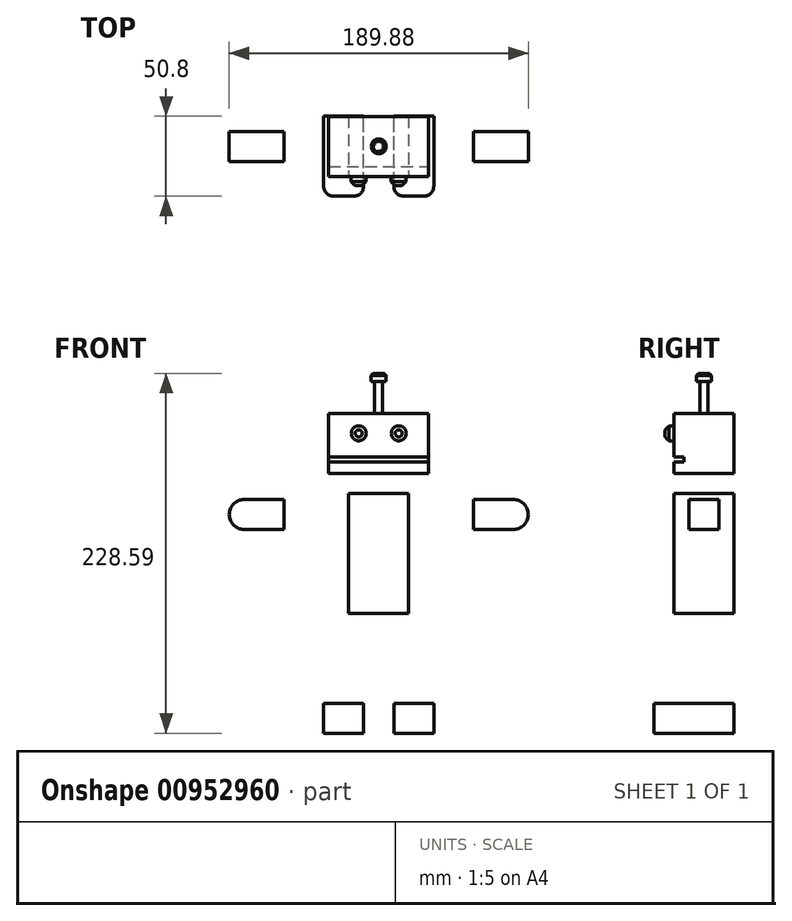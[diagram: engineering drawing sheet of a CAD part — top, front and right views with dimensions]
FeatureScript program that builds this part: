
annotation { "Feature Type Name" : "Feature", "Feature Type Description" : "" }
export const myFeature = defineFeature(function(context is Context, id is Id, definition is map)
    precondition{}
    {
        {
            var Q0;
            Q0=qCreatedBy(makeId("Top.planeOp"),FACE);
            var sketch = newSketch(context, id + "F0", { "sketchPlane" : qUnion([Q0])});
            skLineSegment(sketch, "E0.bottom", {"start": v(-19.05, 19.05) * mm, "end": v(19.05, 19.05) * mm});
            skLineSegment(sketch, "E0.top", {"start": v(-19.05, -19.05) * mm, "end": v(19.05, -19.05) * mm});
            skLineSegment(sketch, "E0.left", {"start": v(-19.05, 19.05) * mm, "end": v(-19.05, -19.05) * mm});
            skLineSegment(sketch, "E0.right", {"start": v(19.05, 19.05) * mm, "end": v(19.05, -19.05) * mm});
            skSolve(sketch);
        }
        {
            var Q0;
            Q0=makeQuery(id+"F0.imprint","IMPRINT",FACE,{"disambiguationData":[TD([[makeQuery(id+"F0.imprint","IMPRINT",EDGE,{"derivedFrom":sQuery(id+"F0.wireOp",EDGE,"E0.bottom")}),-1.0]])]});
            extrude(context, id + "F1", {"entities" : qUnion([Q0]), "depth" : 76.2 * mm, "offsetDistance" : 25.4 * mm});
        }
        {
            var Q0;
            Q0=qCreatedBy(makeId("Front.planeOp"),FACE);
            var sketch = newSketch(context, id + "F2", { "sketchPlane" : qUnion([Q0])});
            skLineSegment(sketch, "E1.bottom", {"start": v(-31.75, 126.99) * mm, "end": v(31.75, 126.99) * mm});
            skLineSegment(sketch, "E1.top", {"start": v(-31.75, 88.89) * mm, "end": v(31.75, 88.89) * mm});
            skLineSegment(sketch, "E1.left", {"start": v(-31.75, 126.99) * mm, "end": v(-31.75, 88.89) * mm});
            skLineSegment(sketch, "E1.right", {"start": v(31.75, 126.99) * mm, "end": v(31.75, 88.89) * mm});
            skSolve(sketch);
        }
        {
            var Q0;
            Q0=makeQuery(id+"F2.imprint","IMPRINT",FACE,{"disambiguationData":[TD([[makeQuery(id+"F2.imprint","IMPRINT",EDGE,{"derivedFrom":sQuery(id+"F2.wireOp",EDGE,"E1.bottom")}),-1.0]])]});
            extrude(context, id + "F3", {"entities" : qUnion([Q0]), "depth" : 19.05 * mm, "offsetDistance" : 25.4 * mm, "hasSecondDirection" : true, "secondDirectionOppositeDirection" : true, "secondDirectionDepth" : 19.05 * mm});
        }
        {
            var Q0;
            Q0=makeQuery(id+"F3.opExtrude","SWEPT_FACE",FACE,{"disambiguationData":[OSD([sQuery(id+"F2.wireOp",EDGE,"E1.right")])]});
            var sketch = newSketch(context, id + "F4", { "sketchPlane" : qUnion([Q0])});
            skLineSegment(sketch, "E2.bottom", {"start": v(-19.05, 96.06) * mm, "end": v(-12.7, 96.06) * mm});
            skLineSegment(sketch, "E2.top", {"start": v(-19.05, 99.24) * mm, "end": v(-12.7, 99.24) * mm});
            skLineSegment(sketch, "E2.left", {"start": v(-19.05, 96.06) * mm, "end": v(-19.05, 99.24) * mm});
            skLineSegment(sketch, "E2.right", {"start": v(-12.7, 96.06) * mm, "end": v(-12.7, 99.24) * mm});
            skSolve(sketch);
        }
        {
            var Q0;
            Q0=makeQuery(id+"F4.imprint","IMPRINT",FACE,{"disambiguationData":[TD([[makeQuery(id+"F4.imprint","IMPRINT",EDGE,{"derivedFrom":sQuery(id+"F4.wireOp",EDGE,"E2.bottom")}),1.0]])]});
            extrude(context, id + "F5", {"entities" : qUnion([Q0]), "operationType" : NewBodyOperationType.REMOVE, "endBound" : BoundingType.THROUGH_ALL, "oppositeDirection" : true, "depth" : 25.4 * mm, "offsetDistance" : 25.4 * mm});
        }
        {
            var Q0;
            {var subQ0=sQuery(id+"F2.wireOp",EDGE,"E1.bottom");var subQ1=sQuery(id+"F2.wireOp",EDGE,"E1.right");var subQ2=sQuery(id+"F2.wireOp",EDGE,"E1.left");Q0=makeQuery(id+"F5.boolean.opBoolean","SPLIT",FACE,{"disambiguationData":[TD([makeQuery(id+"F3.opExtrude","SWEPT_FACE",FACE,{"disambiguationData":[OSD([subQ0])]})])],"derivedFrom":makeQuery(id+"F3.opExtrude","CAP_FACE",FACE,{"disambiguationData":[OSD([subQ0,sQuery(id+"F2.wireOp",EDGE,"E1.top"),subQ2,subQ1])],"isStart":false})});}
            var sketch = newSketch(context, id + "F6", { "sketchPlane" : qUnion([Q0])});
            skCircle(sketch, "E3", {"center": v(-12.7, 114.29) * mm, "radius": 4.76 * mm});
            skCircle(sketch, "E4", {"center": v(12.7, 114.29) * mm, "radius": 4.76 * mm});
            skLineSegment(sketch, "E5", {"start": v(0, 134.8) * mm, "end": v(0, 83.98) * mm, "construction": true});
            skSolve(sketch);
        }
        {
            var Q0;
            Q0 = qSketchRegion(id + "F6", true);
            extrude(context, id + "F7", {"entities" : qUnion([Q0]), "depth" : 5.84 * mm, "offsetDistance" : 25.4 * mm});
        }
        {
            var Q0;
            Q0=makeQuery(id+"F7.opExtrude","CAP_EDGE",EDGE,{"disambiguationData":[OSD([sQuery(id+"F6.wireOp",EDGE,"E3")])],"isStart":false});
            var Q1;
            Q1=makeQuery(id+"F7.opExtrude","CAP_FACE",FACE,{"disambiguationData":[OSD([sQuery(id+"F6.wireOp",EDGE,"E4")])],"isStart":false});
            chamfer(context, id + "F8", {"entities" : qUnion([Q0, Q1]), "width" : 2.54 * mm, "tangentPropagation" : true});
        }
        {
            var Q0;
            Q0=makeQuery(id+"F3.opExtrude","SWEPT_FACE",FACE,{"disambiguationData":[OSD([sQuery(id+"F2.wireOp",EDGE,"E1.bottom")])]});
            var sketch = newSketch(context, id + "F9", { "sketchPlane" : qUnion([Q0])});
            skCircle(sketch, "E6", {"center": v(0, 0) * mm, "radius": 2.54 * mm});
            skSolve(sketch);
        }
        {
            var Q0;
            Q0 = qSketchRegion(id + "F9", true);
            extrude(context, id + "F10", {"entities" : qUnion([Q0]), "operationType" : NewBodyOperationType.ADD, "depth" : 20.32 * mm, "offsetDistance" : 25.4 * mm});
        }
        {
            var Q0;
            Q0=makeQuery(id+"F10.opExtrude","CAP_FACE",FACE,{"disambiguationData":[OSD([sQuery(id+"F9.wireOp",EDGE,"E6")])],"isStart":false});
            var sketch = newSketch(context, id + "F11", { "sketchPlane" : qUnion([Q0])});
            skCircle(sketch, "E7", {"center": v(0, 0) * mm, "radius": 4.76 * mm});
            skSolve(sketch);
        }
        {
            var Q0;
            Q0=makeQuery(id+"F11.imprint","IMPRINT",FACE,{"disambiguationData":[TD([[makeQuery(id+"F11.imprint","IMPRINT",EDGE,{"derivedFrom":sQuery(id+"F11.wireOp",EDGE,"E7")}),1.0]])]});
            var Q1;
            Q1=makeQuery(id+"F11.imprint","IMPRINT",FACE,{"disambiguationData":[TD([[makeQuery(id+"F11.imprint","IMPRINT",EDGE,{"derivedFrom":makeQuery(id+"F10.opExtrude","CAP_EDGE",EDGE,{"disambiguationData":[OSD([sQuery(id+"F9.wireOp",EDGE,"E6")])],"isStart":false})}),1.0]])]});
            extrude(context, id + "F12", {"entities" : qUnion([Q0, Q1]), "operationType" : NewBodyOperationType.ADD, "depth" : 5.08 * mm, "offsetDistance" : 25.4 * mm});
        }
        {
            var Q0;
            Q0=makeQuery(id+"F12.opExtrude","CAP_EDGE",EDGE,{"disambiguationData":[OSD([sQuery(id+"F11.wireOp",EDGE,"E7")])],"isStart":false});
            chamfer(context, id + "F13", {"entities" : qUnion([Q0]), "width" : 1.27 * mm, "tangentPropagation" : true});
        }
        {
            var Q0;
            Q0=qCreatedBy(makeId("Top.planeOp"),FACE);
            cPlane(context, id + "F14", {"entities" : qUnion([Q0]), "cplaneType" : CPlaneType.OFFSET, "offset" : 76.2 * mm, "oppositeDirection" : true, "width" : 152.4 * mm, "height" : 152.4 * mm});
        }
        {
            var Q0;
            Q0=qCreatedBy(id+"F14.planeOp",FACE);
            var sketch = newSketch(context, id + "F15", { "sketchPlane" : qUnion([Q0])});
            skLineSegment(sketch, "E8.bottom", {"start": v(-28.6, -31.7) * mm, "end": v(-15.9, -31.7) * mm});
            skLineSegment(sketch, "E8.top", {"start": v(-34.96, 19.1) * mm, "end": v(-9.56, 19.1) * mm});
            skLineSegment(sketch, "E8.left", {"start": v(-34.96, -25.35) * mm, "end": v(-34.96, 19.1) * mm});
            skLineSegment(sketch, "E8.right", {"start": v(-9.56, -25.35) * mm, "end": v(-9.56, 19.1) * mm});
            skPoint(sketch, "E9.visualSharp", {"position": v(-34.96, -31.7) * mm});
            skArc(sketch, "E9.filletArc", {"start": v(-34.96, -25.35) * mm, "mid": v(-33.1, -29.84) * mm, "end": v(-28.6, -31.7) * mm});
            skPoint(sketch, "E10.visualSharp", {"position": v(-9.56, -31.7) * mm});
            skArc(sketch, "E10.filletArc", {"start": v(-15.9, -31.7) * mm, "mid": v(-11.42, -29.84) * mm, "end": v(-9.56, -25.35) * mm});
            skLineSegment(sketch, "E11.MirrorCS", {"start": v(34.96, 19.1) * mm, "end": v(9.56, 19.1) * mm});
            skArc(sketch, "E12.MirrorCS", {"start": v(15.9, -31.7) * mm, "mid": v(11.42, -29.84) * mm, "end": v(9.56, -25.35) * mm});
            skPoint(sketch, "E13.MirrorP", {"position": v(34.96, -31.7) * mm});
            skArc(sketch, "E14.MirrorCS", {"start": v(34.96, -25.35) * mm, "mid": v(33.1, -29.84) * mm, "end": v(28.6, -31.7) * mm});
            skPoint(sketch, "E15.MirrorP", {"position": v(9.56, -31.7) * mm});
            skLineSegment(sketch, "E16.MirrorCS", {"start": v(34.96, -25.35) * mm, "end": v(34.96, 19.1) * mm});
            skLineSegment(sketch, "E17.MirrorCS", {"start": v(28.6, -31.7) * mm, "end": v(15.9, -31.7) * mm});
            skLineSegment(sketch, "E18.MirrorCS", {"start": v(9.56, -25.35) * mm, "end": v(9.56, 19.1) * mm});
            skSolve(sketch);
        }
        {
            var Q0;
            Q0=makeQuery(id+"F15.imprint","IMPRINT",FACE,{"disambiguationData":[TD([[makeQuery(id+"F15.imprint","IMPRINT",EDGE,{"derivedFrom":sQuery(id+"F15.wireOp",EDGE,"E8.bottom")}),1.0]])]});
            var Q1;
            Q1=makeQuery(id+"F15.imprint","IMPRINT",FACE,{"disambiguationData":[TD([[makeQuery(id+"F15.imprint","IMPRINT",EDGE,{"derivedFrom":sQuery(id+"F15.wireOp",EDGE,"E11.MirrorCS")}),1.0]])]});
            extrude(context, id + "F16", {"entities" : qUnion([Q0, Q1]), "depth" : 19.05 * mm, "offsetDistance" : 25.4 * mm});
        }
        {
            var Q0;
            Q0=qCreatedBy(makeId("Front.planeOp"),FACE);
            var sketch = newSketch(context, id + "F17", { "sketchPlane" : qUnion([Q0])});
            skLineSegment(sketch, "E19.bottom", {"start": v(-85.41, 72.3) * mm, "end": v(-60.01, 72.3) * mm});
            skLineSegment(sketch, "E19.top", {"start": v(-85.41, 53.25) * mm, "end": v(-60.01, 53.25) * mm});
            skLineSegment(sketch, "E19.right", {"start": v(-60.01, 72.3) * mm, "end": v(-60.01, 53.25) * mm});
            skArc(sketch, "E20", {"start": v(-85.41, 72.3) * mm, "mid": v(-94.94, 62.78) * mm, "end": v(-85.41, 53.25) * mm});
            skLineSegment(sketch, "E21.MirrorCS", {"start": v(85.41, 72.3) * mm, "end": v(60.01, 72.3) * mm});
            skLineSegment(sketch, "E22.MirrorCS", {"start": v(85.41, 53.25) * mm, "end": v(60.01, 53.25) * mm});
            skLineSegment(sketch, "E23.MirrorCS", {"start": v(60.01, 72.3) * mm, "end": v(60.01, 53.25) * mm});
            skArc(sketch, "E24.MirrorCS", {"start": v(85.41, 72.3) * mm, "mid": v(94.94, 62.78) * mm, "end": v(85.41, 53.25) * mm});
            skSolve(sketch);
        }
        {
            var Q0;
            Q0 = qSketchRegion(id + "F17", true);
            extrude(context, id + "F18", {"entities" : qUnion([Q0]), "depth" : 9.52 * mm, "offsetDistance" : 25.4 * mm, "hasSecondDirection" : true, "secondDirectionOppositeDirection" : true, "secondDirectionDepth" : 9.52 * mm});
        }
    });
